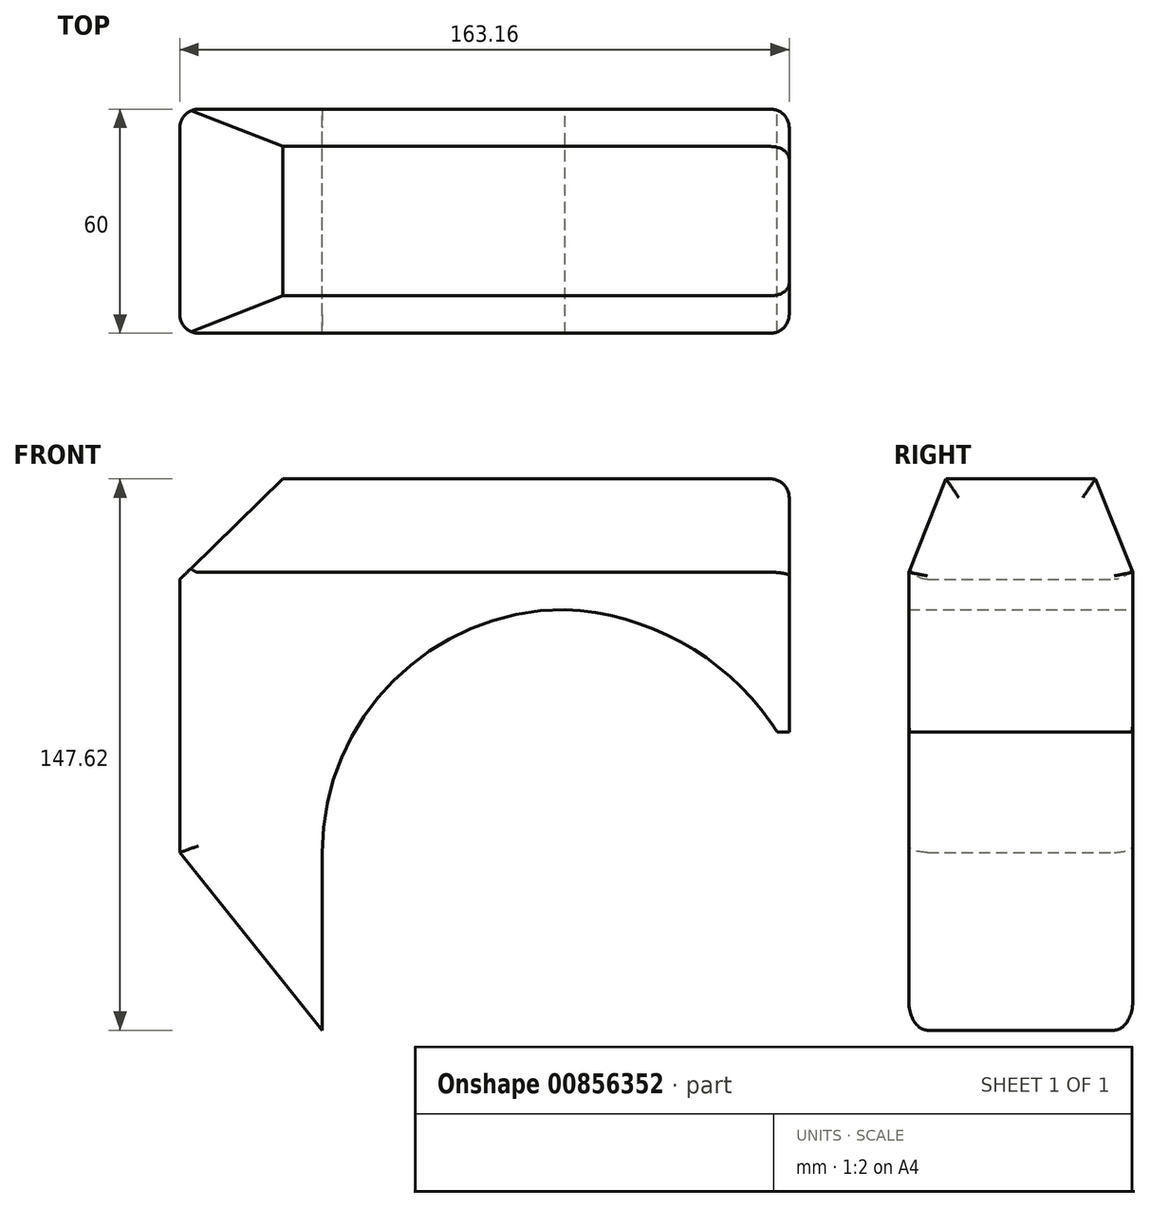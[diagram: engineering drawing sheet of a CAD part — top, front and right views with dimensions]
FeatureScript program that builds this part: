
annotation { "Feature Type Name" : "Feature", "Feature Type Description" : "" }
export const myFeature = defineFeature(function(context is Context, id is Id, definition is map)
    precondition{}
    {
        {
            var Q0;
            Q0=qCreatedBy(makeId("Front.planeOp"),FACE);
            var sketch = newSketch(context, id + "F0", { "sketchPlane" : qUnion([Q0])});
            skLineSegment(sketch, "E0", {"start": v(125, 75) * mm, "end": v(125, 100) * mm});
            skLineSegment(sketch, "E1", {"start": v(-38.16, 110.03) * mm, "end": v(-38.19, 110) * mm});
            skPoint(sketch, "E2", {"position": v(65, 65) * mm});
            skPoint(sketch, "E3", {"position": v(0, 0) * mm});
            skArc(sketch, "E4", {"start": v(65, 65) * mm, "mid": v(19.04, 45.96) * mm, "end": v(0, 0) * mm});
            skLineSegment(sketch, "E5", {"start": v(125, 75) * mm, "end": v(125, 32.2) * mm});
            skLineSegment(sketch, "E6", {"start": v(125, 32.2) * mm, "end": v(121.8, 32.2) * mm});
            skArc(sketch, "E7", {"start": v(121.8, 32.2) * mm, "mid": v(97.42, 55.55) * mm, "end": v(65, 65) * mm});
            skLineSegment(sketch, "E8", {"start": v(-38.16, 0) * mm, "end": v(-38.16, 73.1) * mm});
            skLineSegment(sketch, "E9", {"start": v(-38.16, 73.1) * mm, "end": v(-10.58, 100) * mm});
            skLineSegment(sketch, "E10", {"start": v(-10.58, 100) * mm, "end": v(125, 100) * mm});
            skLineSegment(sketch, "E11", {"start": v(-38.16, 0) * mm, "end": v(0, -47.62) * mm});
            skLineSegment(sketch, "E12", {"start": v(0, -47.62) * mm, "end": v(0, 0) * mm});
            skSolve(sketch);
        }
        {
            var Q0;
            Q0=makeQuery(id+"F0.imprint","IMPRINT",FACE,{"disambiguationData":[TD([[makeQuery(id+"F0.imprint","IMPRINT",EDGE,{"derivedFrom":sQuery(id+"F0.wireOp",EDGE,"E0")}),1.0]])]});
            extrude(context, id + "F1", {"entities" : qUnion([Q0]), "depth" : 60 * mm, "offsetDistance" : 25 * mm});
        }
        {
            var Q0;
            Q0=makeQuery(id+"F1.opExtrude","CAP_EDGE",EDGE,{"disambiguationData":[OSD([sQuery(id+"F0.wireOp",EDGE,"E10")])],"isStart":false});
            var Q1;
            Q1=makeQuery(id+"F1.opExtrude","CAP_EDGE",EDGE,{"disambiguationData":[OSD([sQuery(id+"F0.wireOp",EDGE,"E10")])],"isStart":true});
            chamfer(context, id + "F2", {"entities" : qUnion([Q0, Q1]), "chamferType" : ChamferType.TWO_OFFSETS, "width1" : 10 * mm, "oppositeDirection" : false, "width2" : 25 * mm, "tangentPropagation" : true});
        }
        {
            var Q0;
            Q0=makeQuery(id+"F1.opExtrude","SWEPT_EDGE",EDGE,{"disambiguationData":[OSD([sQuery(id+"F0.wireOp",EDGE,"E0"),sQuery(id+"F0.wireOp",EDGE,"E10")])]});
            var Q1;
            Q1=makeQuery(id+"F1.opExtrude","CAP_EDGE",EDGE,{"disambiguationData":[OSD([sQuery(id+"F0.wireOp",EDGE,"E0"),sQuery(id+"F0.wireOp",EDGE,"E5")])],"isStart":false});
            var Q2;
            Q2=makeQuery(id+"F1.opExtrude","CAP_EDGE",EDGE,{"disambiguationData":[OSD([sQuery(id+"F0.wireOp",EDGE,"E0"),sQuery(id+"F0.wireOp",EDGE,"E5")])],"isStart":true});
            var Q3;
            Q3=makeQuery(id+"F1.opExtrude","CAP_EDGE",EDGE,{"disambiguationData":[OSD([sQuery(id+"F0.wireOp",EDGE,"E8")])],"isStart":false});
            var Q4;
            Q4=makeQuery(id+"F1.opExtrude","CAP_EDGE",EDGE,{"disambiguationData":[OSD([sQuery(id+"F0.wireOp",EDGE,"E8")])],"isStart":true});
            var Q5;
            Q5=makeQuery(id+"F1.opExtrude","CAP_EDGE",EDGE,{"disambiguationData":[OSD([sQuery(id+"F0.wireOp",EDGE,"E11")])],"isStart":true});
            var Q6;
            Q6=makeQuery(id+"F1.opExtrude","CAP_EDGE",EDGE,{"disambiguationData":[OSD([sQuery(id+"F0.wireOp",EDGE,"E11")])],"isStart":false});
            var Q7;
            Q7=makeQuery(id+"F2.opChamfer","BLEND_EDGE",EDGE,{"blendedFrom":[makeQuery(id+"F1.opExtrude","CAP_EDGE",EDGE,{"disambiguationData":[OSD([sQuery(id+"F0.wireOp",EDGE,"E10")])],"isStart":true}),makeQuery(id+"F1.opExtrude","SWEPT_FACE",FACE,{"disambiguationData":[OSD([sQuery(id+"F0.wireOp",EDGE,"E0"),sQuery(id+"F0.wireOp",EDGE,"E5")])]})],"blendedInto":[makeQuery(id+"F1.opExtrude","SWEPT_FACE",FACE,{"disambiguationData":[OSD([sQuery(id+"F0.wireOp",EDGE,"E0"),sQuery(id+"F0.wireOp",EDGE,"E5")])]})]});
            var Q8;
            Q8=makeQuery(id+"F2.opChamfer","BLEND_EDGE",EDGE,{"blendedFrom":[makeQuery(id+"F1.opExtrude","CAP_EDGE",EDGE,{"disambiguationData":[OSD([sQuery(id+"F0.wireOp",EDGE,"E10")])],"isStart":false}),makeQuery(id+"F1.opExtrude","SWEPT_FACE",FACE,{"disambiguationData":[OSD([sQuery(id+"F0.wireOp",EDGE,"E0"),sQuery(id+"F0.wireOp",EDGE,"E5")])]})],"blendedInto":[makeQuery(id+"F1.opExtrude","SWEPT_FACE",FACE,{"disambiguationData":[OSD([sQuery(id+"F0.wireOp",EDGE,"E0"),sQuery(id+"F0.wireOp",EDGE,"E5")])]})]});
            fillet(context, id + "F3", {"entities" : qUnion([Q0, Q1, Q2, Q3, Q4, Q5, Q6, Q7, Q8]), "radius" : 5 * mm, "tangentPropagation" : true, "allowEdgeOverflow" : false});
        }
    });
